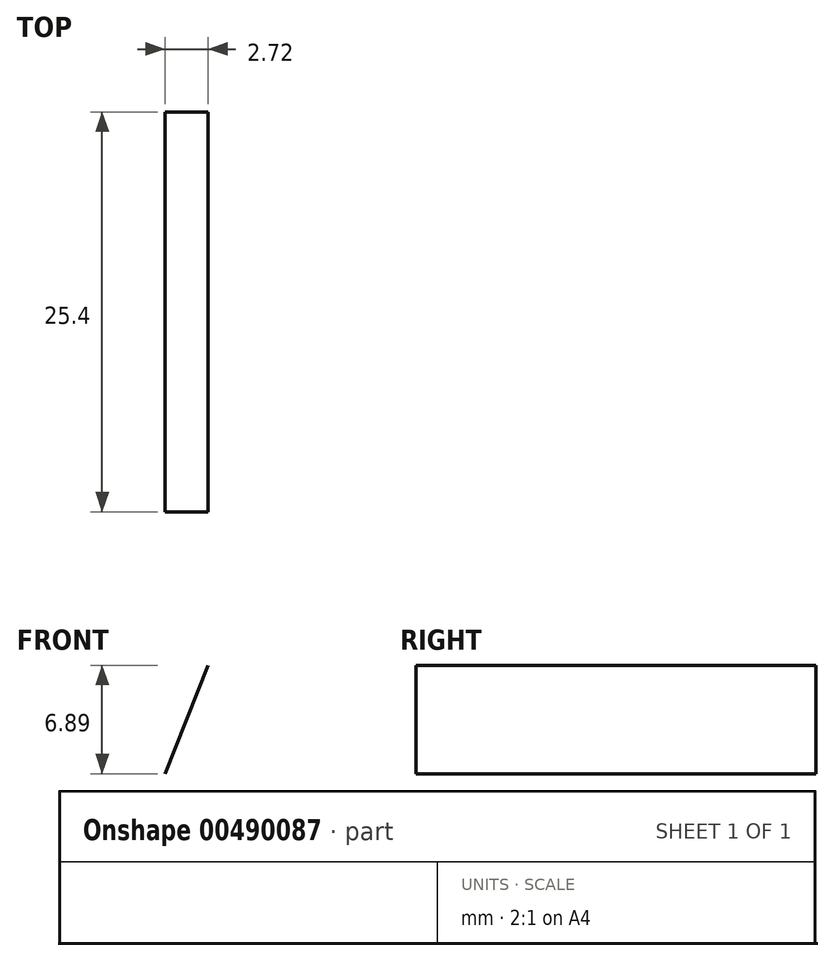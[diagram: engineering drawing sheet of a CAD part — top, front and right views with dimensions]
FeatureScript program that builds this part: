
annotation { "Feature Type Name" : "Feature", "Feature Type Description" : "" }
export const myFeature = defineFeature(function(context is Context, id is Id, definition is map)
    precondition{}
    {
        {
            var Q0;
            Q0=qCreatedBy(makeId("Front.planeOp"),FACE);
            var sketch = newSketch(context, id + "F0", { "sketchPlane" : qUnion([Q0])});
            skLineSegment(sketch, "E0", {"start": v(0, 0) * mm, "end": v(0, 19.17) * mm});
            skLineSegment(sketch, "E1", {"start": v(0, 19.17) * mm, "end": v(-2.72, 12.28) * mm});
            skSolve(sketch);
        }
        {
            var Q0;
            Q0=sQuery(id+"F0.wireOp",EDGE,"E1");
            extrude(context, id + "F1", {"bodyType" : ToolBodyType.SURFACE, "surfaceEntities" : qUnion([Q0]), "depth" : 25.4 * mm});
        }
    });
